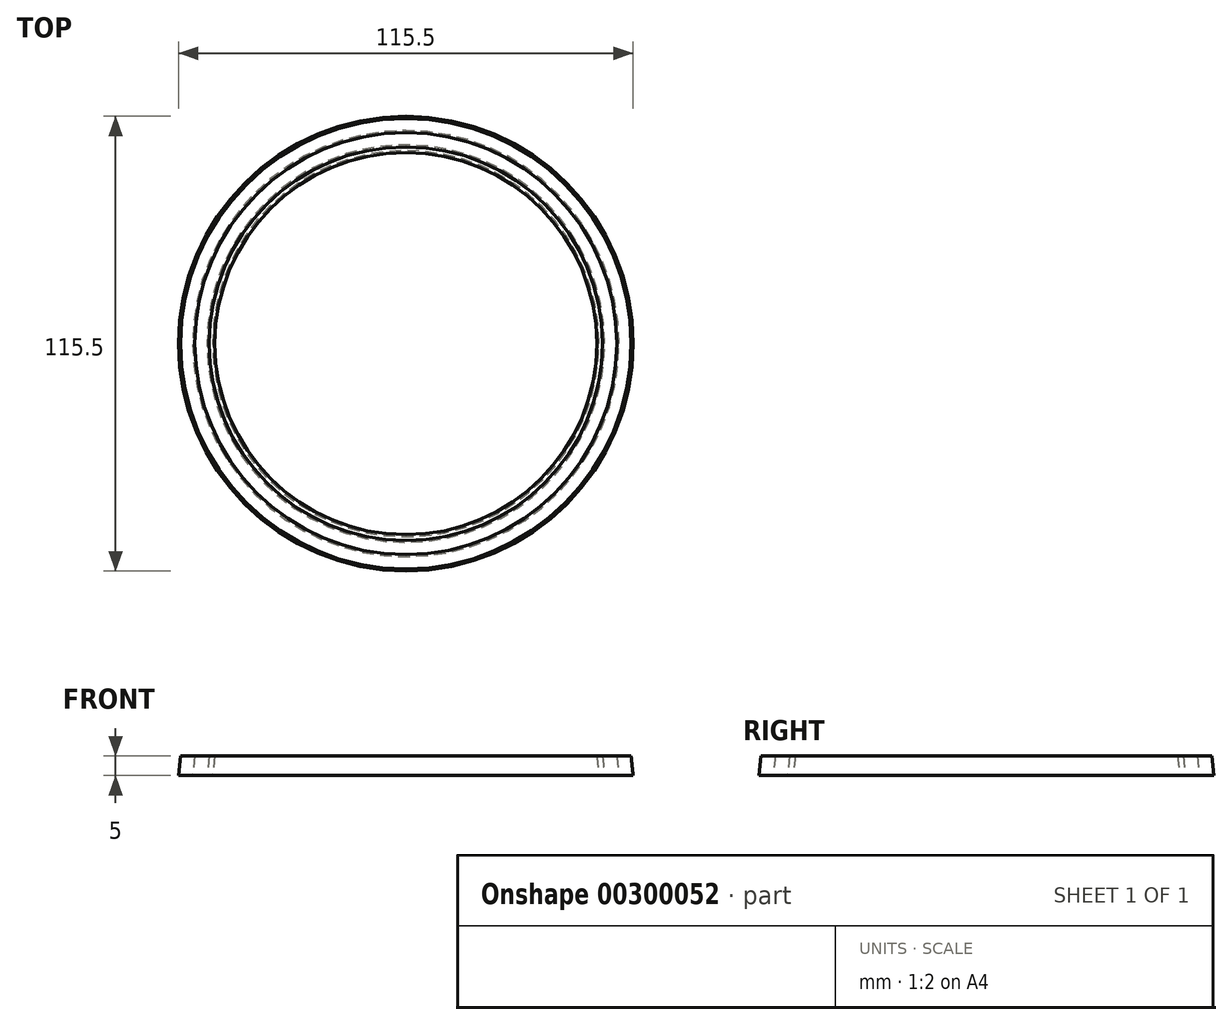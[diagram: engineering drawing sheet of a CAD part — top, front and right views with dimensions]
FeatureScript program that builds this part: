
annotation { "Feature Type Name" : "Feature", "Feature Type Description" : "" }
export const myFeature = defineFeature(function(context is Context, id is Id, definition is map)
    precondition{}
    {
        {
            assignVariable(context, id + "F0", {"name" : "bucket_t", "anyValue" : 0.75});
        }
        {
            assignVariable(context, id + "F1", {"name" : "bucket_top_d", "anyValue" : 117 - (getVariable(context, 'bucket_t') * 2)});
        }
        {
            assignVariable(context, id + "F2", {"name" : "bucket_bot_d", "anyValue" : 88 - (getVariable(context, 'bucket_t') * 2)});
        }
        {
            assignVariable(context, id + "F3", {"name" : "bucket_h", "anyValue" : 140});
        }
        {
            assignVariable(context, id + "F4", {"name" : "bucket_angle", "anyValue" : atan(((getVariable(context, 'bucket_top_d') - getVariable(context, 'bucket_bot_d')) / 2) / getVariable(context, 'bucket_h'))});
        }
        {
            assignVariable(context, id + "F5", {"name" : "spacer_h", "anyValue" : 5});
        }
        {
            var Q0;
            Q0=qCreatedBy(makeId("Top.planeOp"),FACE);
            var sketch = newSketch(context, id + "F6", { "sketchPlane" : qUnion([Q0])});
            skCircle(sketch, "E0", {"center": v(0, 0) * mm, "radius": 57.75 * mm});
            skSolve(sketch);
        }
        {
            var Q0;
            Q0 = qSketchRegion(id + "F6", true);
            extrude(context, id + "F7", {"entities" : qUnion([Q0]), "depth" : (getVariable(context, 'spacer_h')) * mm, "hasDraft" : true, "draftAngle" : getVariable(context, 'bucket_angle'), "draftPullDirection" : true});
        }
        {
            var Q0;
            Q0=qCreatedBy(makeId("Top.planeOp"),FACE);
            var sketch = newSketch(context, id + "F8", { "sketchPlane" : qUnion([Q0])});
            skCircle(sketch, "E1", {"center": v(0, 0) * mm, "radius": 54.12 * mm});
            skSolve(sketch);
        }
        {
            var Q0;
            Q0 = qSketchRegion(id + "F8", true);
            extrude(context, id + "F9", {"entities" : qUnion([Q0]), "depth" : (getVariable(context, 'spacer_h')) * mm, "hasDraft" : true, "draftAngle" : getVariable(context, 'bucket_angle'), "draftPullDirection" : true});
        }
        {
            var Q0;
            Q0=qCreatedBy(makeId("Top.planeOp"),FACE);
            var sketch = newSketch(context, id + "F10", { "sketchPlane" : qUnion([Q0])});
            skCircle(sketch, "E2", {"center": v(0, 0) * mm, "radius": 50.5 * mm});
            skSolve(sketch);
        }
        {
            var Q0;
            Q0 = qSketchRegion(id + "F10", true);
            extrude(context, id + "F11", {"entities" : qUnion([Q0]), "depth" : (getVariable(context, 'spacer_h')) * mm, "hasDraft" : true, "draftAngle" : getVariable(context, 'bucket_angle'), "draftPullDirection" : true});
        }
        {
            var Q0;
            Q0=qCreatedBy(makeId("Top.planeOp"),FACE);
            var sketch = newSketch(context, id + "F12", { "sketchPlane" : qUnion([Q0])});
            skCircle(sketch, "E3", {"center": v(0, 0) * mm, "radius": 49.05 * mm});
            skSolve(sketch);
        }
        {
            var Q0;
            Q0=makeQuery(id+"F12.imprint","IMPRINT",FACE,{"disambiguationData":[TD([[makeQuery(id+"F12.imprint","IMPRINT",EDGE,{"derivedFrom":sQuery(id+"F12.wireOp",EDGE,"E3")}),1.0]])]});
            extrude(context, id + "F13", {"entities" : qUnion([Q0]), "depth" : (getVariable(context, 'spacer_h')) * mm, "hasDraft" : true, "draftAngle" : getVariable(context, 'bucket_angle'), "draftPullDirection" : true});
        }
    });
